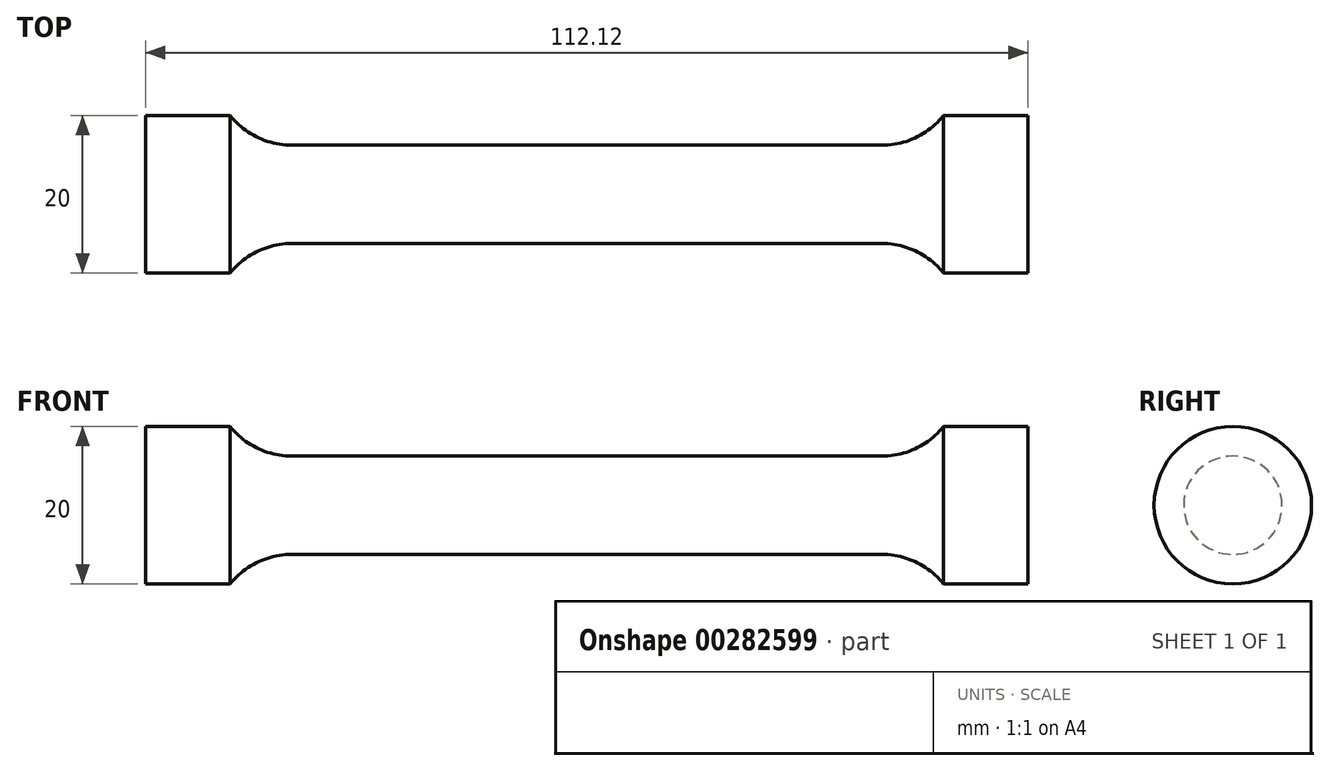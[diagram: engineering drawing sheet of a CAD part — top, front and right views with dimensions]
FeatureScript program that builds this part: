
annotation { "Feature Type Name" : "Feature", "Feature Type Description" : "" }
export const myFeature = defineFeature(function(context is Context, id is Id, definition is map)
    precondition{}
    {
        {
            var Q0;
            Q0=qCreatedBy(makeId("Front.planeOp"),FACE);
            var sketch = newSketch(context, id + "F0", { "sketchPlane" : qUnion([Q0])});
            skLineSegment(sketch, "E0", {"start": v(0, 6.25) * mm, "end": v(37.5, 6.25) * mm});
            skArc(sketch, "E1", {"start": v(37.5, 6.25) * mm, "mid": v(41.83, 7.24) * mm, "end": v(45.3, 10) * mm});
            skLineSegment(sketch, "E2", {"start": v(45.3, 10) * mm, "end": v(56.06, 10) * mm});
            skLineSegment(sketch, "E3", {"start": v(56.06, 10) * mm, "end": v(56.06, 0) * mm});
            skLineSegment(sketch, "E4", {"start": v(56.06, 0) * mm, "end": v(0, 0) * mm});
            skLineSegment(sketch, "E5.MirrorCS", {"start": v(0, 6.25) * mm, "end": v(-37.5, 6.25) * mm});
            skLineSegment(sketch, "E6.MirrorCS", {"start": v(-56.06, 0) * mm, "end": v(0, 0) * mm});
            skLineSegment(sketch, "E7.MirrorCS", {"start": v(-45.3, 10) * mm, "end": v(-56.06, 10) * mm});
            skLineSegment(sketch, "E8.MirrorCS", {"start": v(-56.06, 10) * mm, "end": v(-56.06, 0) * mm});
            skArc(sketch, "E9.MirrorCS", {"start": v(-37.5, 6.25) * mm, "mid": v(-41.83, 7.24) * mm, "end": v(-45.3, 10) * mm});
            skSolve(sketch);
        }
        {
            var Q0;
            Q0=makeQuery(id+"F0.imprint","IMPRINT",FACE,{"disambiguationData":[TD([[makeQuery(id+"F0.imprint","IMPRINT",EDGE,{"derivedFrom":sQuery(id+"F0.wireOp",EDGE,"E0")}),-1.0]])]});
            var Q1;
            Q1=sQuery(id+"F0.wireOp",EDGE,"E6.MirrorCS");
            revolve(context, id + "F1", {"entities" : qUnion([Q0]), "axis" : qUnion([Q1]), "revolveType" : RevolveType.FULL});
        }
    });
